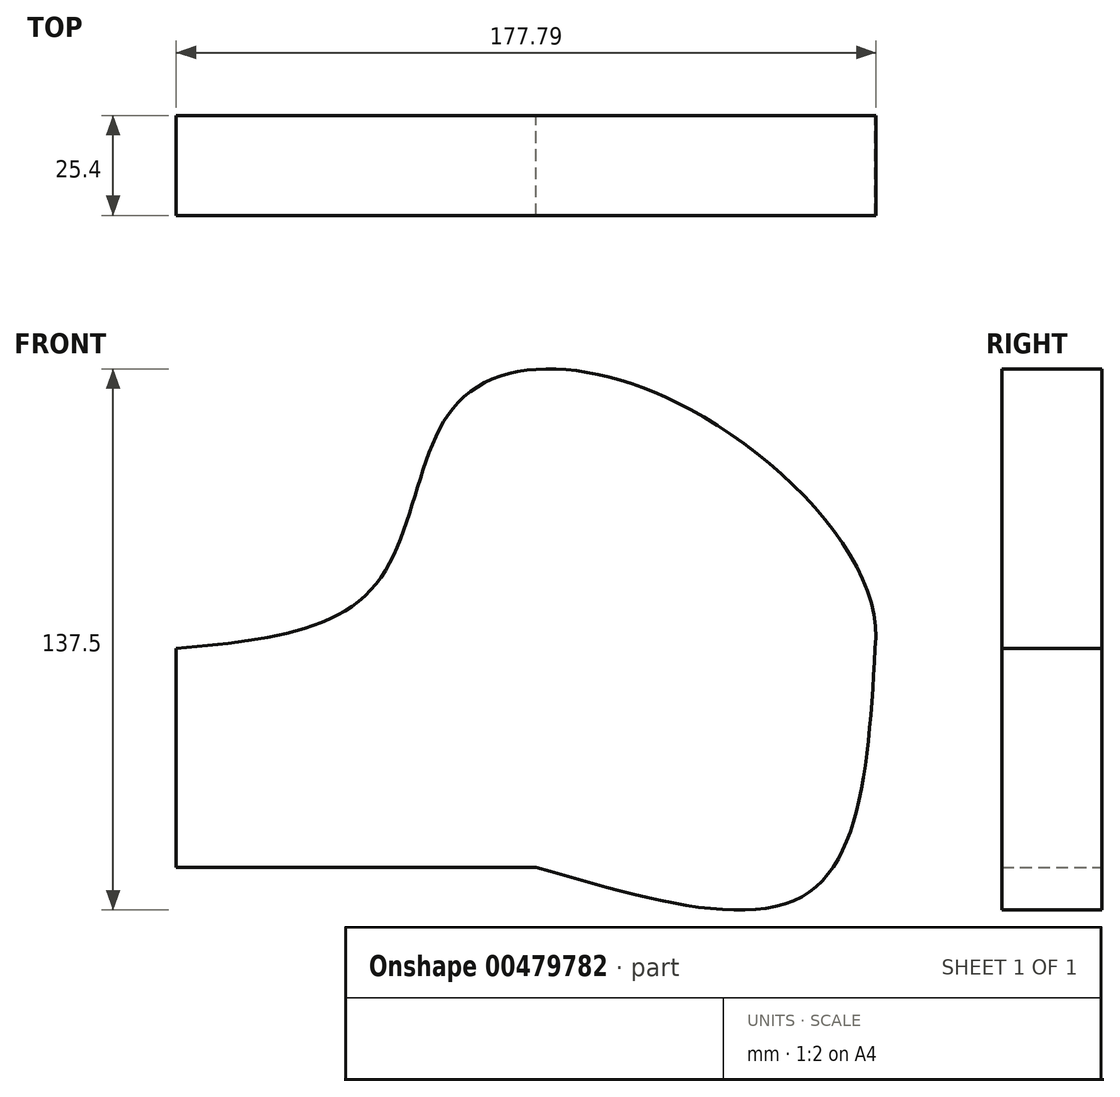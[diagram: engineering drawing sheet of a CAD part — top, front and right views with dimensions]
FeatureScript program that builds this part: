
annotation { "Feature Type Name" : "Feature", "Feature Type Description" : "" }
export const myFeature = defineFeature(function(context is Context, id is Id, definition is map)
    precondition{}
    {
        {
            var Q0;
            Q0=qCreatedBy(makeId("Front.planeOp"),FACE);
            var sketch = newSketch(context, id + "F0", { "sketchPlane" : qUnion([Q0])});
            skLineSegment(sketch, "E0.bottom", {"start": v(-45.72, -27.77) * mm, "end": v(45.72, -27.77) * mm});
            skLineSegment(sketch, "E0.top", {"start": v(-45.72, 27.77) * mm, "end": v(45.72, 27.77) * mm});
            skLineSegment(sketch, "E0.left", {"start": v(-45.72, -27.77) * mm, "end": v(-45.72, 27.77) * mm});
            skLineSegment(sketch, "E0.right", {"start": v(45.72, -27.77) * mm, "end": v(45.72, 27.77) * mm});
            skPoint(sketch, "E0.middle", {"position": v(0, 0) * mm});
            skLineSegment(sketch, "E1.bottom", {"start": v(81.42, 44.2) * mm, "end": v(25.89, 44.2) * mm});
            skLineSegment(sketch, "E1.top", {"start": v(81.42, 90.3) * mm, "end": v(25.89, 90.3) * mm});
            skLineSegment(sketch, "E1.left", {"start": v(81.42, 44.2) * mm, "end": v(81.42, 90.3) * mm});
            skLineSegment(sketch, "E1.right", {"start": v(25.89, 44.2) * mm, "end": v(25.89, 90.3) * mm});
            skPoint(sketch, "E1.middle", {"position": v(53.65, 67.26) * mm});
            skLineSegment(sketch, "E2", {"start": v(45.72, 27.77) * mm, "end": v(70.4, 27.77) * mm});
            skArc(sketch, "E3", {"start": v(70.4, 27.77) * mm, "mid": v(80.3, 33.05) * mm, "end": v(81.42, 44.2) * mm});
            skLineSegment(sketch, "E4", {"start": v(25.89, 44.2) * mm, "end": v(5.1, 44.2) * mm});
            skArc(sketch, "E5.0", {"start": v(70.4, 2.37) * mm, "mid": v(101.4, 18.92) * mm, "end": v(104.9, 53.87) * mm});
            skLineSegment(sketch, "E5.1", {"start": v(45.72, 2.37) * mm, "end": v(70.4, 2.37) * mm});
            skLineSegment(sketch, "E6", {"start": v(104.9, 53.87) * mm, "end": v(81.42, 44.2) * mm});
            skLineSegment(sketch, "E7", {"start": v(81.42, 90.3) * mm, "end": v(104.9, 53.87) * mm});
            skFitSpline(sketch, "E8", {"points": [v(-45.72, 27.77) * mm, v(5.1, 44.2) * mm, v(25.89, 90.3) * mm, v(81.42, 90.3) * mm, v(131.84, 27.77) * mm, v(45.72, -27.77) * mm], "startDerivative": vector(341.5, 31.58) * mm, "endDerivative": vector(-501.9, -190.63) * mm});
            skFitSpline(sketch, "E9", {"points": [v(87.07, -12.07) * mm, v(115.13, -34.09) * mm], "startDerivative": vector(28.06, -22.02) * mm, "endDerivative": vector(28.06, -22.02) * mm});
            skFitSpline(sketch, "E10", {"points": [v(45.72, -27.77) * mm, v(115.13, -34.09) * mm, v(131.84, 27.77) * mm], "startDerivative": vector(161.96, -47.8) * mm, "endDerivative": vector(9.2, 160.34) * mm});
            skSolve(sketch);
        }
        {
            var Q0;
            {var subQ0=sQuery(id+"F0.wireOp",EDGE,"E1.top");Q0=makeQuery(id+"F0.imprint","IMPRINT",FACE,{"disambiguationData":[TD([[makeQuery(id+"F0.imprint","IMPRINT",EDGE,{"derivedFrom":subQ0}),-1.0]])]});}
            var Q1;
            {var subQ0=sQuery(id+"F0.wireOp",EDGE,"E10");var subQ4=makeQuery(id+"F0.imprint","IMPRINT",VERTEX,{"derivedFrom":subQ0});Q1=makeQuery(id+"F0.imprint","IMPRINT",FACE,{"disambiguationData":[TD([[makeQuery(id+"F0.imprint","IMPRINT",EDGE,{"disambiguationData":[TD([[subQ4,-1.0]])],"derivedFrom":subQ0}),1.0]])]});}
            var Q2;
            {var subQ0=sQuery(id+"F0.wireOp",EDGE,"E1.right");Q2=makeQuery(id+"F0.imprint","IMPRINT",FACE,{"disambiguationData":[TD([[makeQuery(id+"F0.imprint","IMPRINT",EDGE,{"derivedFrom":subQ0}),1.0]])]});}
            var Q3;
            {var subQ1=sQuery(id+"F0.wireOp",EDGE,"E0.bottom");Q3=makeQuery(id+"F0.imprint","IMPRINT",FACE,{"disambiguationData":[TD([[makeQuery(id+"F0.imprint","IMPRINT",EDGE,{"derivedFrom":subQ1}),1.0]])]});}
            var Q4;
            Q4=makeQuery(id+"F0.imprint","IMPRINT",FACE,{"disambiguationData":[TD([[makeQuery(id+"F0.imprint","IMPRINT",EDGE,{"derivedFrom":sQuery(id+"F0.wireOp",EDGE,"E1.left")}),-1.0]])]});
            var Q5;
            {var subQ1=sQuery(id+"F0.wireOp",EDGE,"E0.top");Q5=makeQuery(id+"F0.imprint","IMPRINT",FACE,{"disambiguationData":[TD([[makeQuery(id+"F0.imprint","IMPRINT",EDGE,{"derivedFrom":subQ1}),1.0]])]});}
            var Q6;
            Q6=makeQuery(id+"F0.imprint","IMPRINT",FACE,{"disambiguationData":[TD([[makeQuery(id+"F0.imprint","IMPRINT",EDGE,{"derivedFrom":sQuery(id+"F0.wireOp",EDGE,"E5.0")}),-1.0]])]});
            var Q7;
            Q7=makeQuery(id+"F0.imprint","IMPRINT",FACE,{"disambiguationData":[TD([[makeQuery(id+"F0.imprint","IMPRINT",EDGE,{"derivedFrom":sQuery(id+"F0.wireOp",EDGE,"E1.bottom")}),-1.0]])]});
            var Q8;
            {var subQ0=sQuery(id+"F0.wireOp",EDGE,"E2");Q8=makeQuery(id+"F0.imprint","IMPRINT",FACE,{"disambiguationData":[TD([[makeQuery(id+"F0.imprint","IMPRINT",EDGE,{"derivedFrom":subQ0}),-1.0]])]});}
            extrude(context, id + "F1", {"entities" : qUnion([Q0, Q1, Q2, Q3, Q4, Q5, Q6, Q7, Q8]), "depth" : 25.4 * mm});
        }
    });
